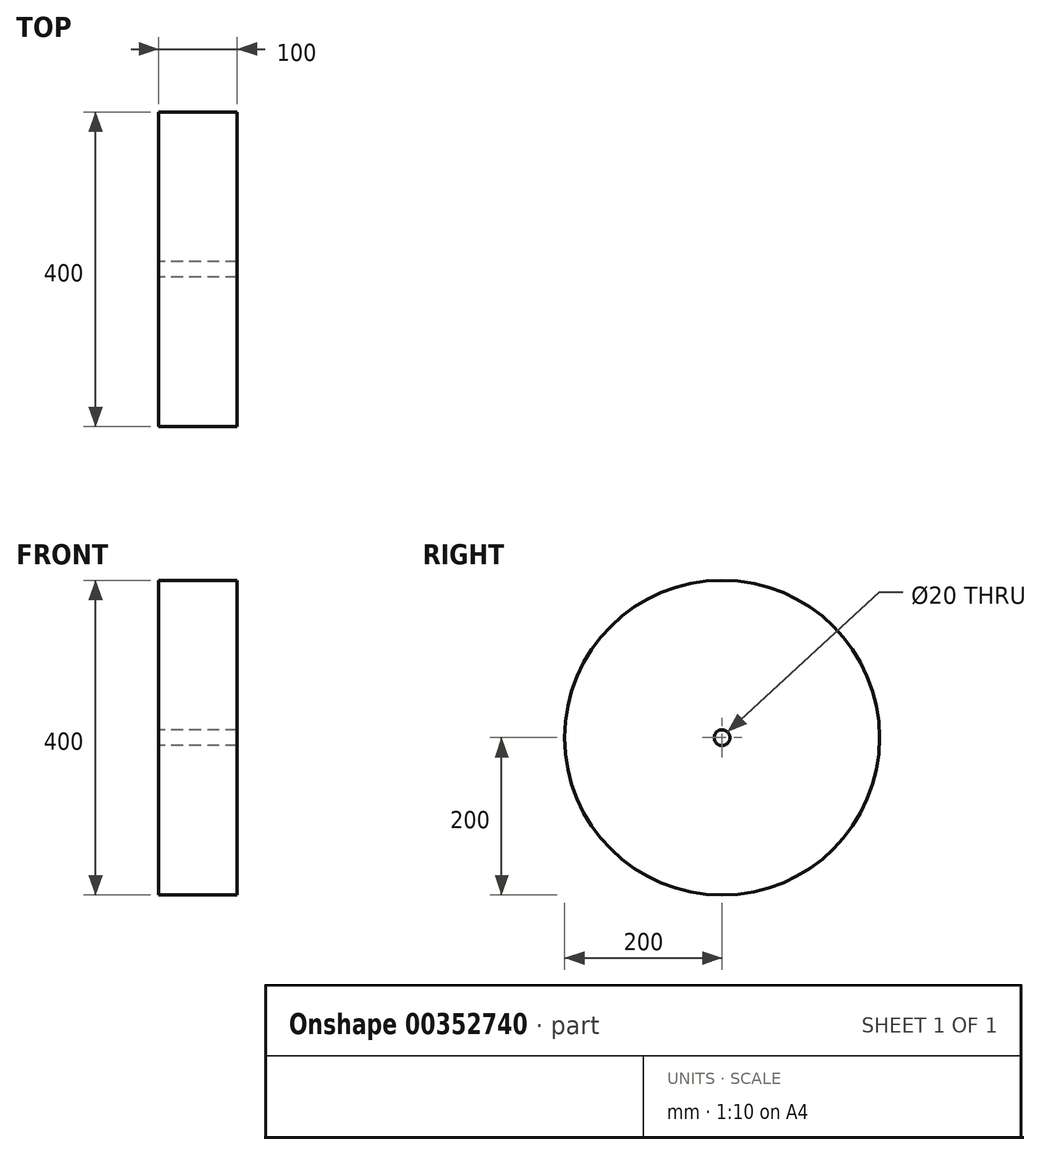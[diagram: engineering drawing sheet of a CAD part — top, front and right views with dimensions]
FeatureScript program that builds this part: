
annotation { "Feature Type Name" : "Feature", "Feature Type Description" : "" }
export const myFeature = defineFeature(function(context is Context, id is Id, definition is map)
    precondition{}
    {
        {
            var Q0;
            Q0=qCreatedBy(makeId("Right.planeOp"),FACE);
            var sketch = newSketch(context, id + "F0", { "sketchPlane" : qUnion([Q0])});
            skCircle(sketch, "E0", {"center": v(0, 0) * mm, "radius": 200 * mm});
            skCircle(sketch, "E1", {"center": v(0, 0) * mm, "radius": 10 * mm});
            skSolve(sketch);
        }
        {
            var Q0;
            Q0 = qSketchRegion(id + "F0", true);
            extrude(context, id + "F1", {"entities" : qUnion([Q0]), "depth" : 100 * mm});
        }
    });
